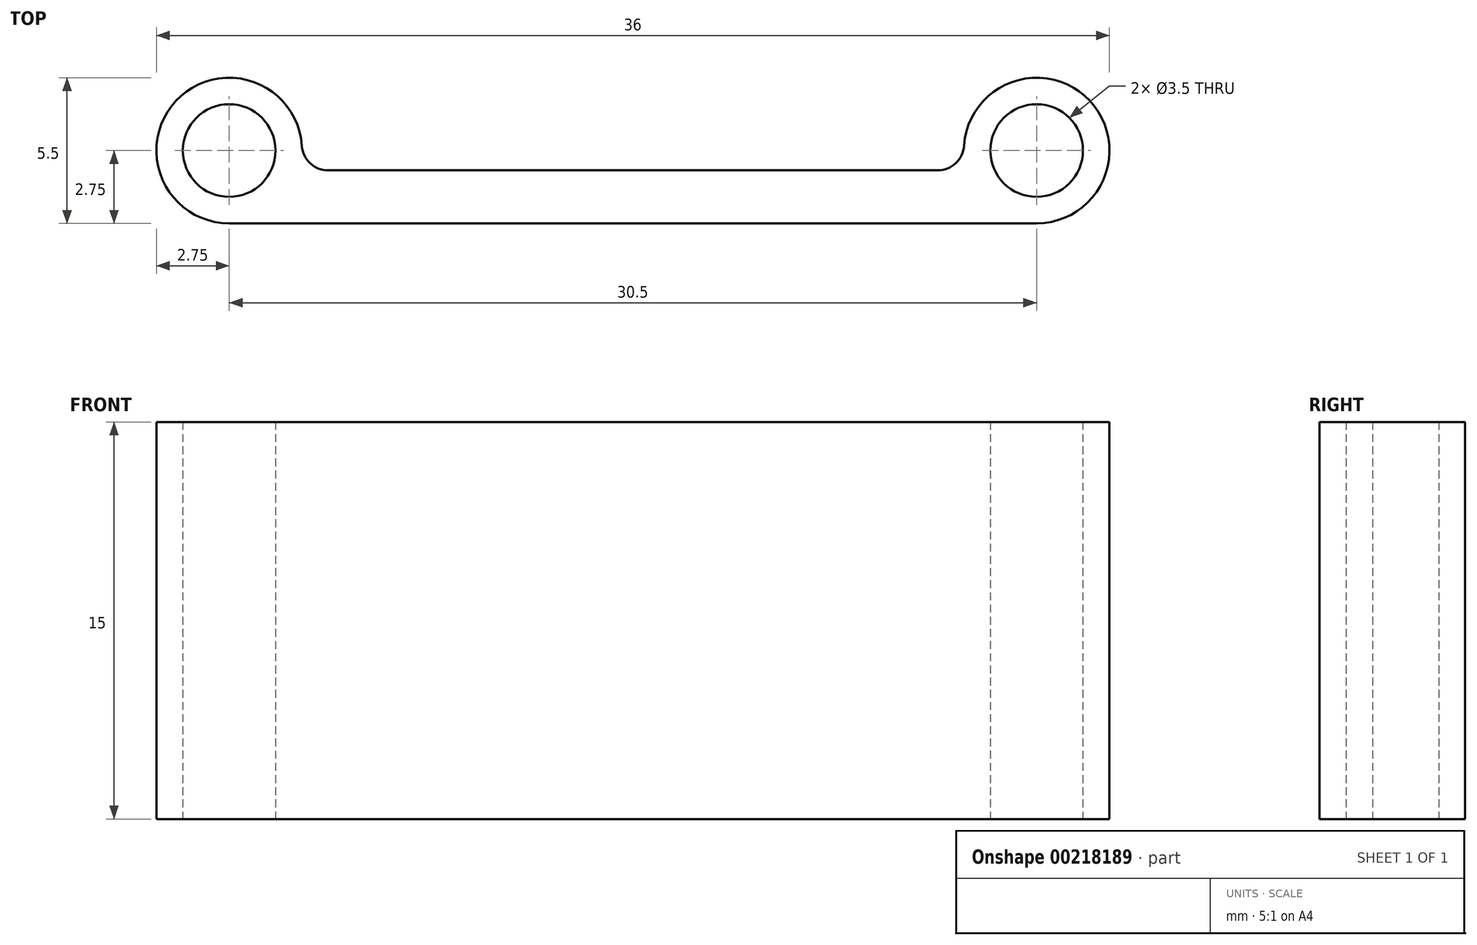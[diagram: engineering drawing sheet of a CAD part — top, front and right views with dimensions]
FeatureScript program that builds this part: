
annotation { "Feature Type Name" : "Feature", "Feature Type Description" : "" }
export const myFeature = defineFeature(function(context is Context, id is Id, definition is map)
    precondition{}
    {
        {
            var Q0;
            Q0=qCreatedBy(makeId("Top.planeOp"),FACE);
            var sketch = newSketch(context, id + "F0", { "sketchPlane" : qUnion([Q0])});
            skArc(sketch, "E0", {"start": v(-12.5, 2.93) * mm, "mid": v(-17.26, 4.63) * mm, "end": v(-15.25, 0) * mm});
            skArc(sketch, "E1", {"start": v(15.25, 0) * mm, "mid": v(17.26, 4.63) * mm, "end": v(12.5, 2.93) * mm});
            skLineSegment(sketch, "E2", {"start": v(-15.25, 0) * mm, "end": v(15.25, 0) * mm});
            skLineSegment(sketch, "E3", {"start": v(-11.5, 2) * mm, "end": v(11.5, 2) * mm});
            skPoint(sketch, "E4.visualSharp", {"position": v(-12.6, 2) * mm});
            skArc(sketch, "E4.filletArc", {"start": v(-12.5, 2.93) * mm, "mid": v(-12.2, 2.27) * mm, "end": v(-11.5, 2) * mm});
            skPoint(sketch, "E5.visualSharp", {"position": v(12.6, 2) * mm});
            skArc(sketch, "E5.filletArc", {"start": v(11.5, 2) * mm, "mid": v(12.2, 2.27) * mm, "end": v(12.5, 2.93) * mm});
            skCircle(sketch, "E6", {"center": v(-15.25, 2.75) * mm, "radius": 1.75 * mm});
            skCircle(sketch, "E7", {"center": v(15.25, 2.75) * mm, "radius": 1.75 * mm});
            skSolve(sketch);
        }
        {
            var Q0;
            Q0=qSketchRegion(id+"F0",true);
            extrude(context, id + "F1", {"entities" : qUnion([Q0]), "depth" : 15 * mm});
        }
    });
